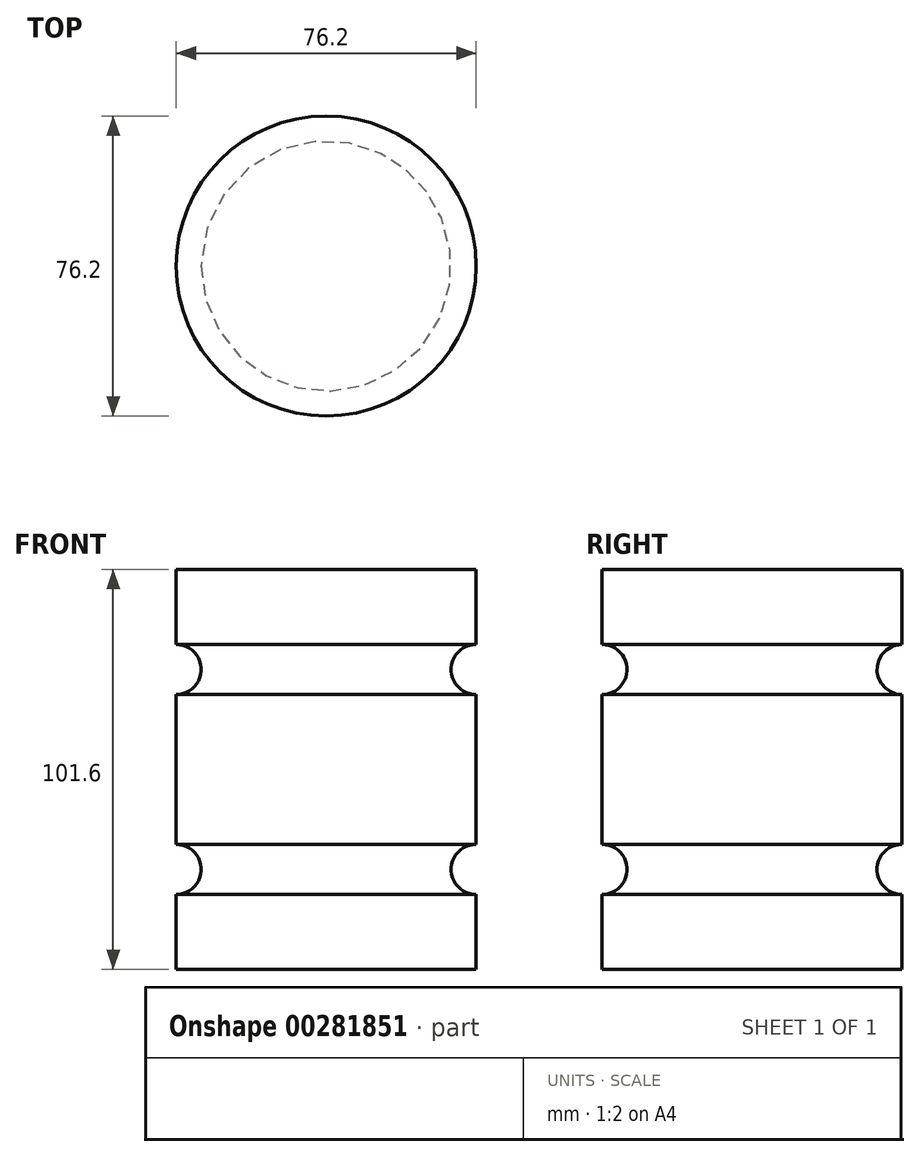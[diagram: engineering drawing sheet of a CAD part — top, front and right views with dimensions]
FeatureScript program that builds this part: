
annotation { "Feature Type Name" : "Feature", "Feature Type Description" : "" }
export const myFeature = defineFeature(function(context is Context, id is Id, definition is map)
    precondition{}
    {
        {
            var Q0;
            Q0=qCreatedBy(makeId("Front.planeOp"),FACE);
            var sketch = newSketch(context, id + "F0", { "sketchPlane" : qUnion([Q0])});
            skLineSegment(sketch, "E0.bottom", {"start": v(0, 0) * mm, "end": v(-38.1, 0) * mm});
            skLineSegment(sketch, "E0.top", {"start": v(0, 101.6) * mm, "end": v(-38.1, 101.6) * mm});
            skLineSegment(sketch, "E0.left", {"start": v(0, 0) * mm, "end": v(0, 19.05) * mm});
            skLineSegment(sketch, "E0.right", {"start": v(-38.1, 0) * mm, "end": v(-38.1, 101.6) * mm});
            skArc(sketch, "E1", {"start": v(0, 82.55) * mm, "mid": v(-6.35, 76.2) * mm, "end": v(0, 69.85) * mm});
            skArc(sketch, "E2", {"start": v(0, 31.75) * mm, "mid": v(-6.35, 25.4) * mm, "end": v(0, 19.05) * mm});
            skLineSegment(sketch, "E3.trimOffspring", {"start": v(0, 82.55) * mm, "end": v(0, 101.6) * mm});
            skLineSegment(sketch, "E4.trimOffspring", {"start": v(0, 31.75) * mm, "end": v(0, 69.85) * mm});
            skSolve(sketch);
        }
        {
            var Q0;
            Q0 = qSketchRegion(id + "F0", true);
            var Q1;
            Q1=sQuery(id+"F0.wireOp",EDGE,"E0.right");
            revolve(context, id + "F1", {"entities" : qUnion([Q0]), "axis" : qUnion([Q1]), "revolveType" : RevolveType.FULL});
        }
    });
